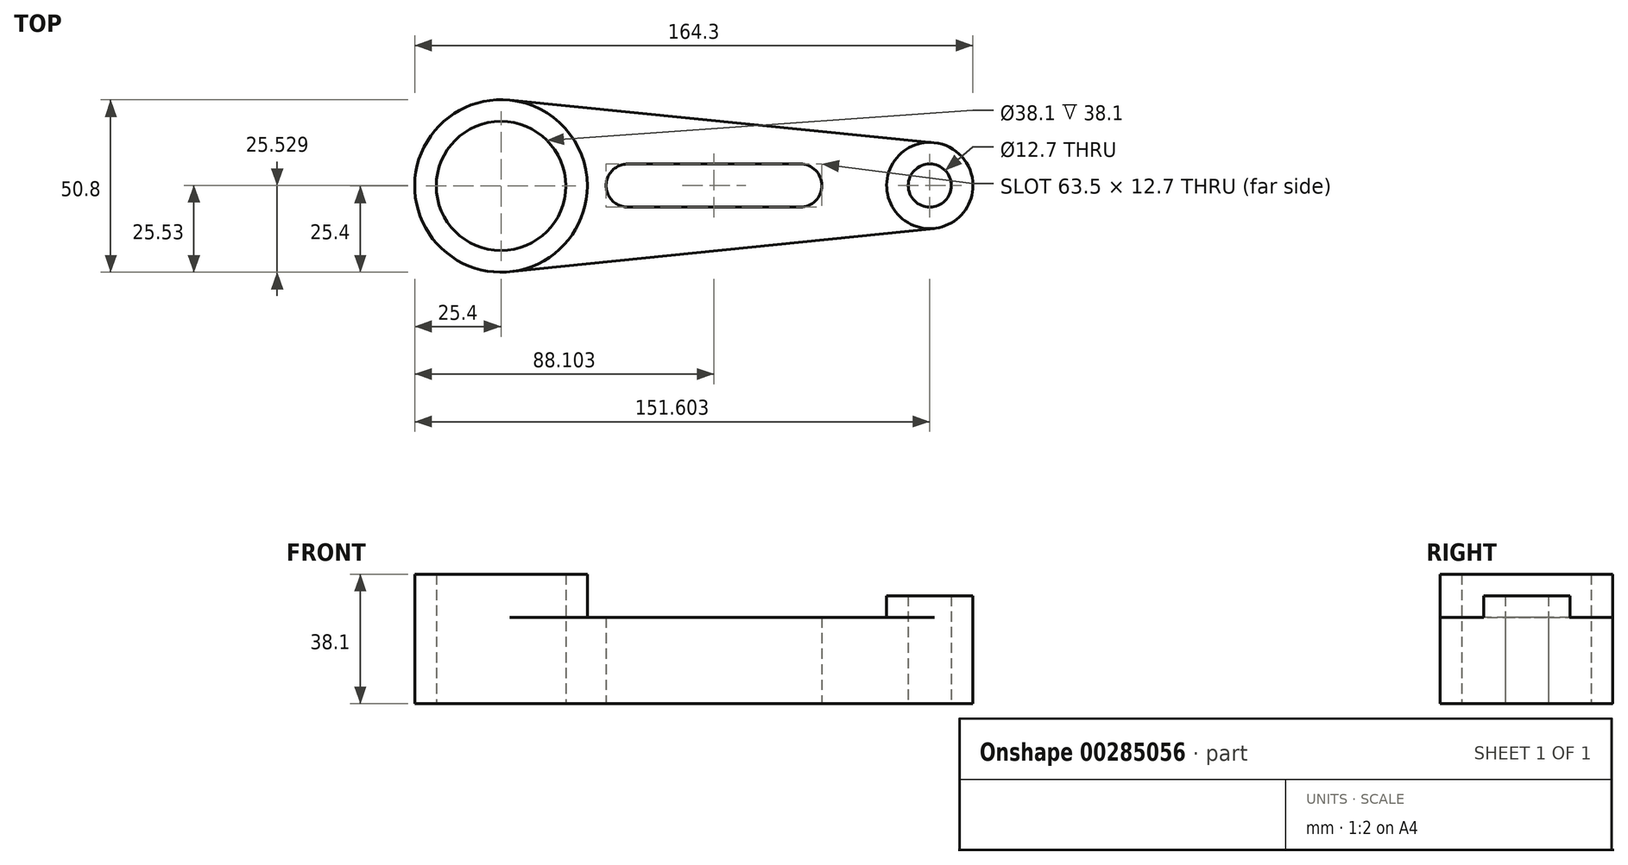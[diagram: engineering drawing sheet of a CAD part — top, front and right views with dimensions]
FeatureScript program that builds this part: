
annotation { "Feature Type Name" : "Feature", "Feature Type Description" : "" }
export const myFeature = defineFeature(function(context is Context, id is Id, definition is map)
    precondition{}
    {
        {
            var Q0;
            Q0=qCreatedBy(makeId("Top.planeOp"),FACE);
            var sketch = newSketch(context, id + "F0", { "sketchPlane" : qUnion([Q0])});
            skCircle(sketch, "E0", {"center": v(0, 0) * mm, "radius": 25.4 * mm});
            skCircle(sketch, "E1", {"center": v(0, 0) * mm, "radius": 19.05 * mm});
            skCircle(sketch, "E2", {"center": v(126.2, 0.13) * mm, "radius": 12.7 * mm});
            skCircle(sketch, "E3", {"center": v(126.2, 0.13) * mm, "radius": 6.35 * mm});
            skLineSegment(sketch, "E4", {"start": v(119.85, 0.13) * mm, "end": v(113.5, 0.13) * mm});
            skArc(sketch, "E5", {"start": v(37.3, 6.48) * mm, "mid": v(30.95, 0.13) * mm, "end": v(37.3, -6.22) * mm});
            skArc(sketch, "E6", {"start": v(88.1, -6.22) * mm, "mid": v(94.45, 0.13) * mm, "end": v(88.1, 6.48) * mm});
            skLineSegment(sketch, "E7", {"start": v(37.3, 6.48) * mm, "end": v(88.1, 6.48) * mm});
            skLineSegment(sketch, "E8", {"start": v(37.3, -6.22) * mm, "end": v(88.1, -6.22) * mm});
            skLineSegment(sketch, "E9", {"start": v(2.53, 25.27) * mm, "end": v(127.47, 12.77) * mm});
            skLineSegment(sketch, "E10", {"start": v(127.5, -12.5) * mm, "end": v(2.58, -25.27) * mm});
            skSolve(sketch);
        }
        {
            var Q0;
            Q0=makeQuery(id+"F0.imprint","IMPRINT",FACE,{"disambiguationData":[TD([[makeQuery(id+"F0.imprint","IMPRINT",EDGE,{"derivedFrom":sQuery(id+"F0.wireOp",EDGE,"E1")}),-1.0]])]});
            extrude(context, id + "F1", {"entities" : qUnion([Q0]), "depth" : 38.1 * mm});
        }
        {
            var Q0;
            Q0=makeQuery(id+"F0.imprint","IMPRINT",FACE,{"disambiguationData":[TD([[makeQuery(id+"F0.imprint","IMPRINT",EDGE,{"derivedFrom":sQuery(id+"F0.wireOp",EDGE,"E5")}),-1.0]])]});
            extrude(context, id + "F2", {"entities" : qUnion([Q0]), "operationType" : NewBodyOperationType.ADD, "depth" : 25.4 * mm});
        }
        {
            var Q0;
            Q0=makeQuery(id+"F0.imprint","IMPRINT",FACE,{"disambiguationData":[TD([[makeQuery(id+"F0.imprint","IMPRINT",EDGE,{"derivedFrom":sQuery(id+"F0.wireOp",EDGE,"E3")}),-1.0]])]});
            extrude(context, id + "F3", {"entities" : qUnion([Q0]), "operationType" : NewBodyOperationType.ADD, "depth" : 31.75 * mm});
        }
    });
